# Revit family: Hager-MINIGAMMA-Surface_mounted-IP30-Without_Cover-With_DIN-Hosted-CH-fr
name_source: partatom
category: Electrical Equipment
units: mm (PartAtom-declared; Revit-internal decimal feet)

## family parameters
Cut with Voids When Loaded = No
Host = Face
Maintain Annotation Orientation = Yes
Panel Configuration = Two Columns, Circuits Across
Part Type = Panelboard
Room Calculation Point = No
Round Connector Dimension = Use Diameter
Shared = No

## types (5) — shared parameters
BC_MODEL_ID = 1554388
BC_OBJECT_ID = 513896
BC_OBJECT_VERSION = #9
Code hager = ADD-EC000214_EU
EF000003 - mode de montage = apparent
EF000024 - résiste aux UV = No
EF000049 - profondeur = 82 mm  [stored 0.269029 ft]
EF000116 - numéro RAL = 9010
EF000118 - avec plaque de montage = No
EF000266 - nombre de rangées = 1
EF001062 - version CEM = No
EF001088 - possibilité de montage adossé = No
EF001134 - rail DIN = Yes
EF005474 - indice de protection (IP) = IP30
EF006244 - couvercle/porte transparente = No
EF006306 - avec serrure = No
EF015941 - porte de transmission du signal = No
ETIM class code = EC000214
ETIM class name = Small distribution board
HG000001-nombre de colonnes = 1
HG000002-avec porte = No
HG000003-Gamme = MINIGAMMA
HG000005-Epaisseur = 2 mm  [stored 0.00656168 ft]
HG000006-Encastré = No
HG000009-Porte à double battant = No
HG000010-Portes asymétriques = No
HG000011-Rangées du bas vides = No
HG000012-Angle de pivotement de la porte = 90.00°
HG000013-Porte à gauche = No
HG000014-Porte à droite = Yes
HG000015-Visibilité de l'emprise de la porte = Yes
HG000016-Visibilité de la porte 3D = Yes
HG000017-Distance entre pôles = 18 mm  [stored 0.0590551 ft]
HG000060-RAL-number = 9010
HG000099-ID modèle Onfly = 507532
HGEF000266-Nombre de rangées = 1
Manufacturer = Hager
Name = MINIGAMMA-Surface_mounted-IP30-Without_Cover-With_DIN-CH
Name BIM&CO = Electricity
Name hager = ADD_Enclosures_EC000214
Uniformat = Low Tension Service & Dist.
Uniformat code = D501001
zero-valued in all types: Default Elevation, EF000218 - profondeur de montage, EF000332 - hauteur d'installation, EF000846 - largeur d'encastrement, EF001131 - profondeur interne, HG000007-Nombre de colonnes vides, HG000008-Nombre de rangées vides

## per-type parameters (varying)
| type | BC_VARIANT_ID | EF000008 - largeur | EF000040 - hauteur | EF002950 - nombre d'unités modulaires | EF015776 - borne de mise à la terre | EF015777 - borne à conducteur neutre | HG000004-Référence fabricant | HGEF0002950-largeur en nombre de modules |
| MINIGAMMA-Surface_mounted_W55_H160_D82_2_Modular_Spacing-GD102N | 1178995 | 55 mm  [stored 0.180446 ft] | 160 mm  [stored 0.524934 ft] | 2 | No | No | GD102N | 2 |
| MINIGAMMA-Surface_mounted_W110_H180_D82_4_Modular_Spacing-GD104N | 1178996 | 110 mm  [stored 0.360892 ft] | 180 mm  [stored 0.590551 ft] | 4 | Yes | Yes | GD104N | 4 |
| MINIGAMMA-Surface_mounted_W146_H180_D82_6_Modular_Spacing-GD106N | 1178997 | 146 mm  [stored 0.479003 ft] | 180 mm  [stored 0.590551 ft] | 6 | No | No | GD106N | 6 |
| MINIGAMMA-Surface_mounted_W182_H180_D82_8_Modular_Spacing-GD108N | 1178998 | 182 mm  [stored 0.597113 ft] | 180 mm  [stored 0.590551 ft] | 8 | No | No | GD108N | 8 |
| MINIGAMMA-Surface_mounted_W218_H180_D82_10_Modular_Spacing-GD110N | 1178999 | 218 mm  [stored 0.715223 ft] | 180 mm  [stored 0.590551 ft] | 10 | No | No | GD110N | 10 |

note: column(s) folded — value = type name in every type: Reference

note: [stored X ft] marks values corroborated as IEEE doubles in the binary element streams (Revit-internal decimal feet)

## geometry (parser evidence)
native form markers: Sweep x14
no freeform markers — native parametric forms only
